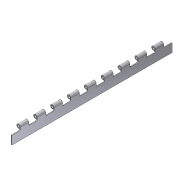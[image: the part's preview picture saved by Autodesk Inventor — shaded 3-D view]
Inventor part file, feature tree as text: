
AUTODESK INVENTOR PART (.ipt)
format: ipt  version: 2012 (Build 160160000, 160)  size: 240,128 bytes
history: native  units: in
note: dims shown in document units (in); Inventor stores cm internally (conversion verified against a paired STEP export)
features: extrude x2, sketch x2, pattern_linear x1, fillet x1, projected_geometry x1
ambient origin geometry x8: Origin, YZ Plane, XZ Plane, XY Plane, X Axis, Y Axis, Z Axis, Center Point
bodies: Solid1 (feature_tree)
feature tree (7):
  extrude  "Extrusion1"  Depth=0.09in
  extrude  "Extrusion2"  Depth=19.0in TaperAngle=0.0deg
  pattern_linear  "Rectangular Pattern1"  Spacing1=1.0in  [1 undecoded]
  fillet  "Fillet2"  Radius=0.125in
  sketch  "Sketch1"  dims[d0=0.445in d1=0.09in]
  sketch  "Sketch2"  dims[d2=0.09in d3=19.0in d4=0.0in d6=1.0in d7=0.125in d8=16.0in d9=0.0in d11=3.937in d13=2.0in d14=0.125in]
  projected_geometry  "Projected Loop1"
note: 1 required parameter value undecoded (feature->parameter linkage not recoverable at this tier; creation-order binding heuristic only, values carry confidence <= 0.55)
